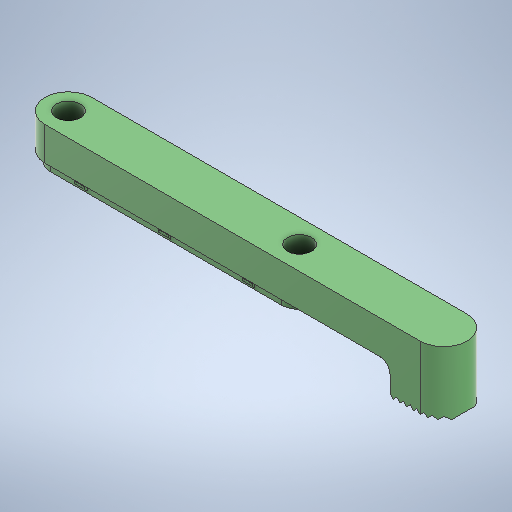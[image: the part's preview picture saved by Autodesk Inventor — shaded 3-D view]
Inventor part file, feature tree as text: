
AUTODESK INVENTOR PART (.ipt)
format: ipt  version: 2025.2 (Build 292293000, 293)  size: 366,080 bytes
history: native  units: mm
features: sketch x6, extrude x5, fillet x4, pattern_linear x1, mirror x1, projected_geometry x1, plane x1
ambient origin geometry x8: Origin, YZ Plane, XZ Plane, XY Plane, X Axis, Y Axis, Z Axis, Center Point
bodies: Solid1 (feature_tree)
feature tree (19):
  extrude  "Extrusion1"  Depth=14.0mm
  fillet  "Fillet1"  Radius=7.2mm
  extrude  "Extrusion2"  Depth=10.0mm TaperAngle=0.0deg
  extrude  "Extrusion3"  Depth=50.0mm
  fillet  "Fillet2"  Radius=1.6mm
  pattern_linear  "Rectangular Pattern1"  Spacing1=0.5mm  [1 undecoded]
  mirror  "Mirror1"
  extrude  "Extrusion4"  Depth=3.0mm TaperAngle=0.0deg
  extrude  "Extrusion5"  Depth=25.0mm
  fillet  "Fillet3"  Radius=0.5mm
  fillet  "Fillet4"  Radius=3.0mm
  sketch  "Sketch1"  dims[d0=14.0mm d1=83.0mm d2=7.2mm]
  sketch  "Sketch2"  dims[d6=7.0mm d7=50.0mm d8=1.6mm]
  sketch  "Sketch4"  dims[d9=3.0mm d10=0.0mm]
  projected_geometry  "Projected Loop1"
  sketch  "Sketch5"  dims[d11=1.0mm]
  plane  "Work Plane1"
  sketch  "Sketch6"  dims[d12=45.0deg d13=0.5mm d14=3.0mm d15=0.0mm d16=30.0mm d18=25.0mm d19=0.5mm d20=3.0mm d21=0.0mm d22=16.0mm d23=1.0mm d24=45.0deg d25=80.0mm d27=2.0mm d28=10.0mm d30=10.0mm d32=8.0mm d33=10.0mm d34=0.0mm d35=7.0mm d36=3.0mm]
  sketch  "Sketch Rectangular Pattern1"  dims[d3=69.0mm d4=10.0mm d5=0.0mm]
note: 1 required parameter value undecoded (feature->parameter linkage not recoverable at this tier; creation-order binding heuristic only, values carry confidence <= 0.55)
